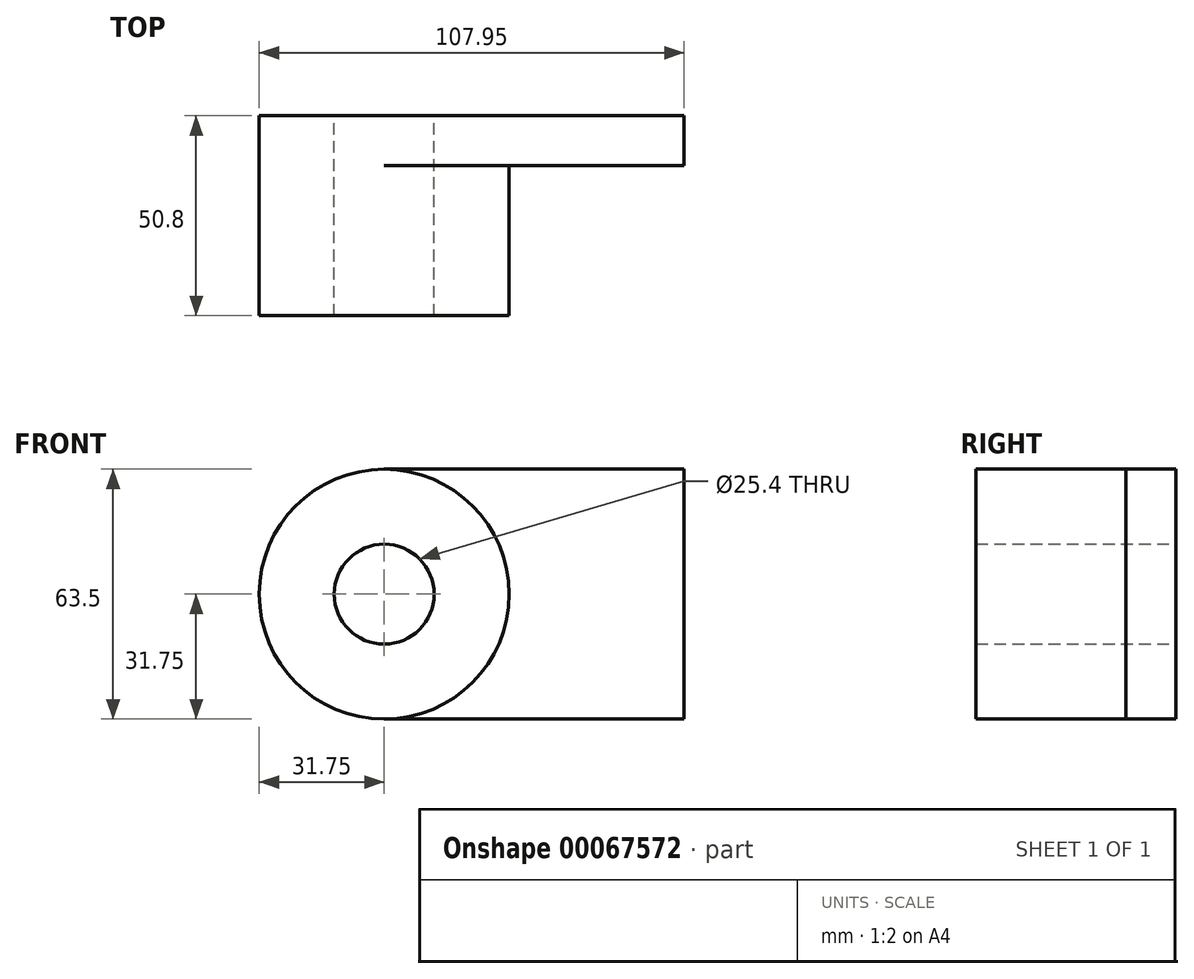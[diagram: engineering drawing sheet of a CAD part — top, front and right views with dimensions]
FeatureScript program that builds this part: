
annotation { "Feature Type Name" : "Feature", "Feature Type Description" : "" }
export const myFeature = defineFeature(function(context is Context, id is Id, definition is map)
    precondition{}
    {
        {
            var Q0;
            Q0=qCreatedBy(makeId("Front.planeOp"),FACE);
            var sketch = newSketch(context, id + "F0", { "sketchPlane" : qUnion([Q0])});
            skLineSegment(sketch, "E0.rect.bottom", {"start": v(-38.1, -31.75) * mm, "end": v(38.1, -31.75) * mm});
            skLineSegment(sketch, "E0.rect.top", {"start": v(-38.1, 31.75) * mm, "end": v(38.1, 31.75) * mm});
            skLineSegment(sketch, "E0.rect.left", {"start": v(-38.1, -31.75) * mm, "end": v(-38.1, 31.75) * mm});
            skLineSegment(sketch, "E0.rect.right", {"start": v(38.1, -31.75) * mm, "end": v(38.1, 31.75) * mm});
            skPoint(sketch, "E0.rect.middle", {"position": v(0, 0) * mm});
            skCircle(sketch, "E1", {"center": v(-38.1, 0) * mm, "radius": 31.75 * mm});
            skCircle(sketch, "E2", {"center": v(-38.1, 0) * mm, "radius": 12.7 * mm});
            skSolve(sketch);
        }
        {
            var Q0;
            {var subQ1=sQuery(id+"F0.wireOp",EDGE,"E0.rect.left");var subQ3=sQuery(id+"F0.wireOp",EDGE,"E2");var subQ4=makeQuery(id+"F0.imprint","INTERSECT",VERTEX,{"disambiguationData":[OD(0.0)],"derivedFrom":[subQ1,subQ3]});Q0=makeQuery(id+"F0.imprint","IMPRINT",FACE,{"disambiguationData":[TD([[makeQuery(id+"F0.imprint","IMPRINT",EDGE,{"disambiguationData":[TD([[subQ4,-1.0]])],"derivedFrom":subQ3}),-1.0]])]});}
            var Q1;
            {var subQ0=sQuery(id+"F0.wireOp",EDGE,"E0.rect.bottom");Q1=makeQuery(id+"F0.imprint","IMPRINT",FACE,{"disambiguationData":[TD([[makeQuery(id+"F0.imprint","IMPRINT",EDGE,{"derivedFrom":subQ0}),1.0]])]});}
            var Q2;
            {var subQ1=sQuery(id+"F0.wireOp",EDGE,"E0.rect.left");var subQ3=sQuery(id+"F0.wireOp",EDGE,"E2");var subQ4=makeQuery(id+"F0.imprint","INTERSECT",VERTEX,{"disambiguationData":[OD(0.0)],"derivedFrom":[subQ1,subQ3]});Q2=makeQuery(id+"F0.imprint","IMPRINT",FACE,{"disambiguationData":[TD([[makeQuery(id+"F0.imprint","IMPRINT",EDGE,{"disambiguationData":[TD([[subQ4,1.0]])],"derivedFrom":subQ3}),-1.0]])]});}
            extrude(context, id + "F1", {"entities" : qUnion([Q0, Q1, Q2]), "depth" : 12.7 * mm});
        }
        {
            var Q0;
            {var subQ1=sQuery(id+"F0.wireOp",EDGE,"E0.rect.left");var subQ3=sQuery(id+"F0.wireOp",EDGE,"E2");var subQ4=makeQuery(id+"F0.imprint","INTERSECT",VERTEX,{"disambiguationData":[OD(0.0)],"derivedFrom":[subQ1,subQ3]});Q0=makeQuery(id+"F0.imprint","IMPRINT",FACE,{"disambiguationData":[TD([[makeQuery(id+"F0.imprint","IMPRINT",EDGE,{"disambiguationData":[TD([[subQ4,-1.0]])],"derivedFrom":subQ3}),-1.0]])]});}
            var Q1;
            {var subQ1=sQuery(id+"F0.wireOp",EDGE,"E0.rect.left");var subQ3=sQuery(id+"F0.wireOp",EDGE,"E2");var subQ4=makeQuery(id+"F0.imprint","INTERSECT",VERTEX,{"disambiguationData":[OD(0.0)],"derivedFrom":[subQ1,subQ3]});Q1=makeQuery(id+"F0.imprint","IMPRINT",FACE,{"disambiguationData":[TD([[makeQuery(id+"F0.imprint","IMPRINT",EDGE,{"disambiguationData":[TD([[subQ4,1.0]])],"derivedFrom":subQ3}),-1.0]])]});}
            extrude(context, id + "F2", {"entities" : qUnion([Q0, Q1]), "operationType" : NewBodyOperationType.ADD, "depth" : 50.8 * mm});
        }
    });
